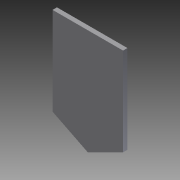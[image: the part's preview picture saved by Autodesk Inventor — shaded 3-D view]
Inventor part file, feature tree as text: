
AUTODESK INVENTOR PART (.ipt)
format: ipt  version: 2012 (Build 160160000, 160)  size: 67,584 bytes
history: native  units: in
note: dims shown in document units (in); Inventor stores cm internally (conversion verified against a paired STEP export)
features: extrude x1, sketch x1
ambient origin geometry x8: Origin, YZ Plane, XZ Plane, XY Plane, X Axis, Y Axis, Z Axis, Center Point
bodies: Solid1 (feature_tree)
feature tree (2):
  extrude  "Extrusion1"  Depth=3.0in
  sketch  "Sketch1"  dims[d0=2.0in d1=3.0in d2=2.5in d3=0.125in d4=0.0in]
